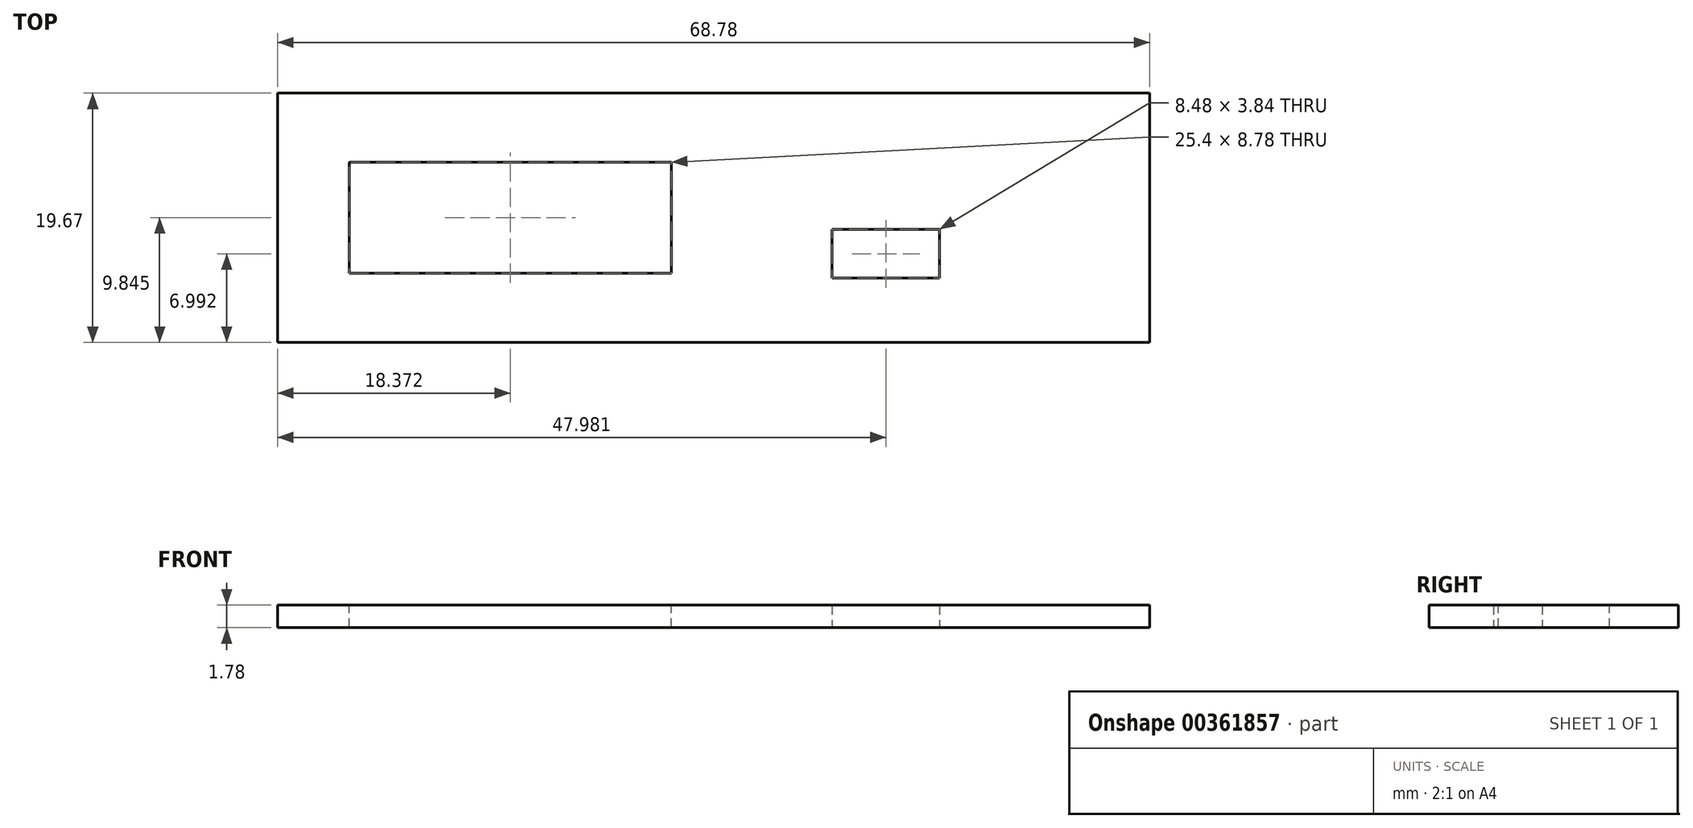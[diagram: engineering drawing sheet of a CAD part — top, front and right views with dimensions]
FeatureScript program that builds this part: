
annotation { "Feature Type Name" : "Feature", "Feature Type Description" : "" }
export const myFeature = defineFeature(function(context is Context, id is Id, definition is map)
    precondition{}
    {
        {
            var Q0;
            Q0=qCreatedBy(makeId("Top.planeOp"),FACE);
            var sketch = newSketch(context, id + "F0", { "sketchPlane" : qUnion([Q0])});
            skLineSegment(sketch, "E0.bottom", {"start": v(0, 0) * mm, "end": v(-68.78, 0) * mm});
            skLineSegment(sketch, "E0.top", {"start": v(0, 19.67) * mm, "end": v(-68.78, 19.67) * mm});
            skLineSegment(sketch, "E0.left", {"start": v(0, 0) * mm, "end": v(0, 19.67) * mm});
            skLineSegment(sketch, "E0.right", {"start": v(-68.78, 0) * mm, "end": v(-68.78, 19.67) * mm});
            skSolve(sketch);
        }
        {
            var Q0;
            Q0=makeQuery(id+"F0.imprint","IMPRINT",FACE,{"disambiguationData":[TD([[makeQuery(id+"F0.imprint","IMPRINT",EDGE,{"derivedFrom":sQuery(id+"F0.wireOp",EDGE,"E0.bottom")}),-1.0]])]});
            extrude(context, id + "F1", {"entities" : qUnion([Q0]), "depth" : 1.78 * mm});
        }
        {
            var Q0;
            Q0=makeQuery(id+"F1.opExtrude","CAP_FACE",FACE,{"disambiguationData":[OSD([sQuery(id+"F0.wireOp",EDGE,"E0.bottom"),sQuery(id+"F0.wireOp",EDGE,"E0.top"),sQuery(id+"F0.wireOp",EDGE,"E0.left"),sQuery(id+"F0.wireOp",EDGE,"E0.right")])],"isStart":false});
            var sketch = newSketch(context, id + "F2", { "sketchPlane" : qUnion([Q0])});
            skLineSegment(sketch, "E1.bottom", {"start": v(-63.1, 14.23) * mm, "end": v(-37.7, 14.23) * mm});
            skLineSegment(sketch, "E1.top", {"start": v(-63.1, 5.46) * mm, "end": v(-37.7, 5.46) * mm});
            skLineSegment(sketch, "E1.left", {"start": v(-63.1, 14.23) * mm, "end": v(-63.1, 5.46) * mm});
            skLineSegment(sketch, "E1.right", {"start": v(-37.7, 14.23) * mm, "end": v(-37.7, 5.46) * mm});
            skSolve(sketch);
        }
        {
            var Q0;
            Q0=makeQuery(id+"F2.imprint","IMPRINT",FACE,{"disambiguationData":[TD([[makeQuery(id+"F2.imprint","IMPRINT",EDGE,{"derivedFrom":sQuery(id+"F2.wireOp",EDGE,"E1.bottom")}),-1.0]])]});
            extrude(context, id + "F3", {"entities" : qUnion([Q0]), "operationType" : NewBodyOperationType.REMOVE, "oppositeDirection" : true, "depth" : 25.4 * mm});
        }
        {
            var Q0;
            Q0=qCreatedBy(makeId("Top.planeOp"),FACE);
            var sketch = newSketch(context, id + "F4", { "sketchPlane" : qUnion([Q0])});
            skLineSegment(sketch, "E2.bottom", {"start": v(-25.04, 8.91) * mm, "end": v(-16.56, 8.91) * mm});
            skLineSegment(sketch, "E2.top", {"start": v(-25.04, 5.07) * mm, "end": v(-16.56, 5.07) * mm});
            skLineSegment(sketch, "E2.left", {"start": v(-25.04, 8.91) * mm, "end": v(-25.04, 5.07) * mm});
            skLineSegment(sketch, "E2.right", {"start": v(-16.56, 8.91) * mm, "end": v(-16.56, 5.07) * mm});
            skSolve(sketch);
        }
        {
            var Q0;
            Q0 = qSketchRegion(id + "F4", true);
            extrude(context, id + "F5", {"entities" : qUnion([Q0]), "operationType" : NewBodyOperationType.REMOVE, "endBound" : BoundingType.THROUGH_ALL, "depth" : 25.4 * mm});
        }
    });
